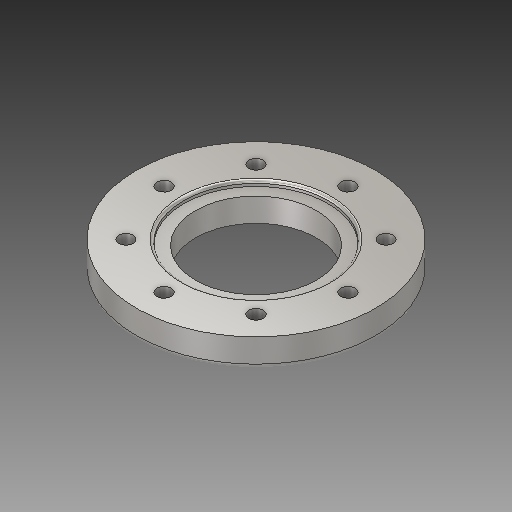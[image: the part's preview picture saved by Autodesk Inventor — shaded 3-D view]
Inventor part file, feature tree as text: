
AUTODESK INVENTOR PART (.ipt)
format: ipt  version: 2019 (Build 230136000, 136)  size: 201,216 bytes
history: native  units: mm
features: hole x3, fillet x2, sketch x2, extrude x1, pattern_circular x1
ambient origin geometry x8: Origin, YZ Plane, XZ Plane, XY Plane, X Axis, Y Axis, Z Axis, Center Point
bodies: Solid1 (feature_tree)
feature tree (9):
  extrude  "Extrusion1"  Depth=11.0mm TaperAngle=0.0deg
  fillet  "Fillet1"  Radius=2.0mm
  hole  "Hole1"  [1 undecoded]
  hole  "Hole2"  [1 undecoded]
  fillet  "Fillet2"  Radius=80.0mm
  hole  "Hole3"  [1 undecoded]
  pattern_circular  "Circular Pattern2"  [2 undecoded]
  sketch  "Sketch1"  dims[d0=91.0mm d1=11.0mm d2=0.0mm d3=2.0mm]
  sketch  "Sketch2"  dims[d4=10.0mm d5=10.0mm d6=46.0mm d7=6.0mm d8=4.0mm d9=2.0mm d10=90.0deg d11=8.0mm d12=20.594885mm d37=10.0mm d38=10.0mm d15=55.0mm d16=6.0mm d17=4.0mm d18=2.0mm d19=90.0deg d20=2.0mm d21=0.0mm d22=1.0mm d23=35.0mm d24=5.5mm d25=6.0mm d26=10.0mm d27=5.0mm d28=90.0deg d29=4.159mm d30=0.0mm d34=80.0mm d35=360.0deg]
note: 5 required parameter values undecoded (feature->parameter linkage not recoverable at this tier; creation-order binding heuristic only, values carry confidence <= 0.55)
